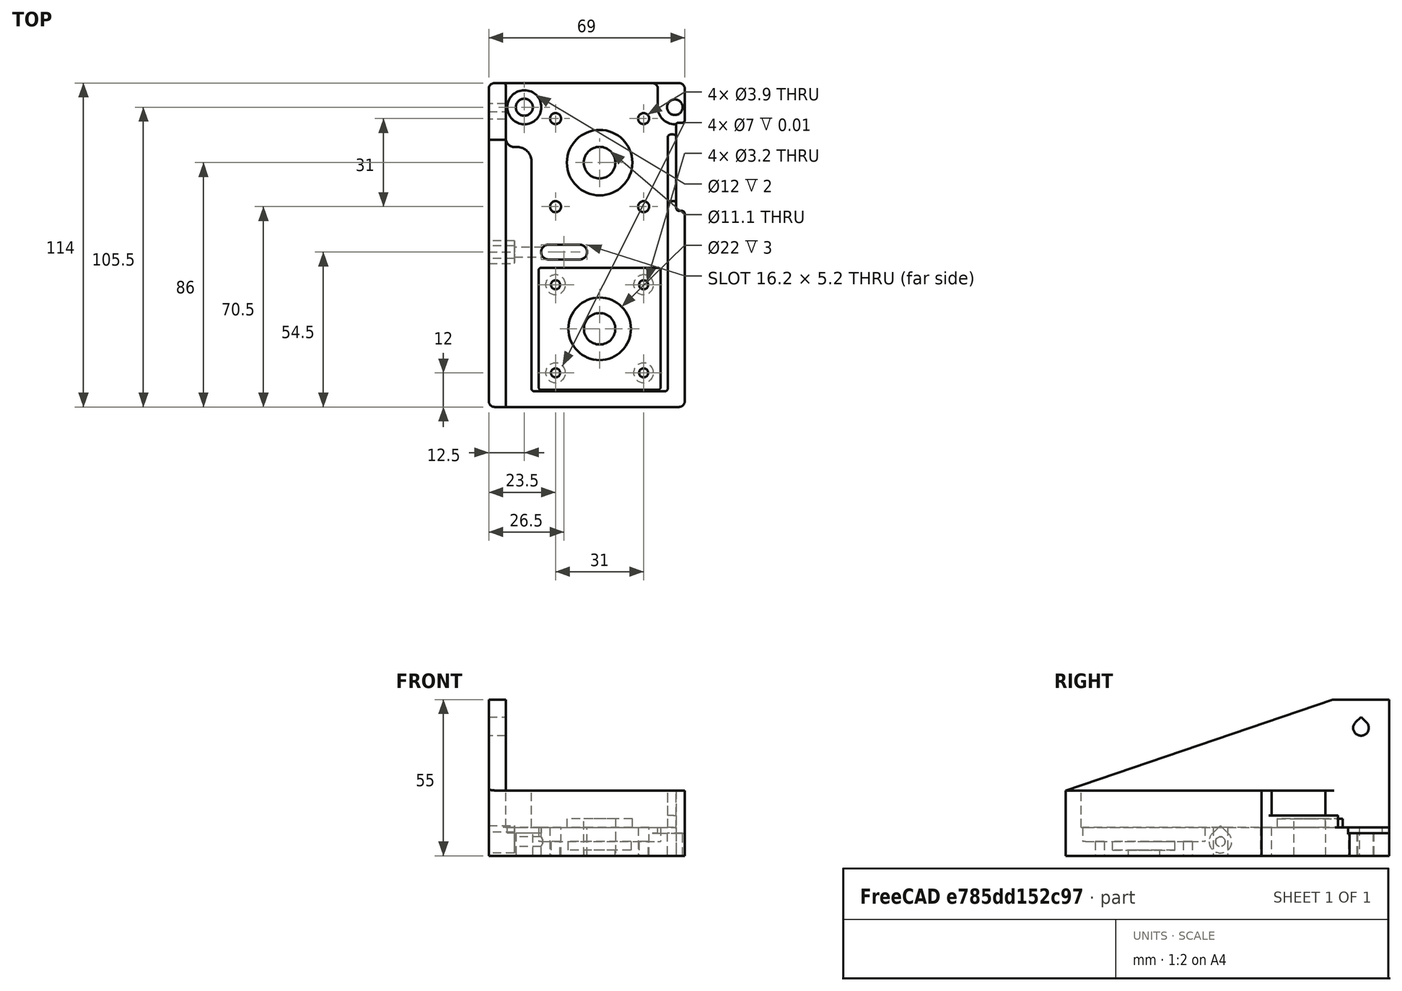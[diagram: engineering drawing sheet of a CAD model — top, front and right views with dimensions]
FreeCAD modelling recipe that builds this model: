
FCSTD DOCUMENT  (FreeCAD 0.19R)
Label: BeltDriveUnit4
License: All rights reserved
LicenseURL: http://en.wikipedia.org/wiki/All_rights_reserved
objects: Sketcher::SketchObject×17, PartDesign::Pocket×12, PartDesign::Fillet×12, PartDesign::Pad×5, PartDesign::Body×1, Mesh::Feature×1
note: 76 computed .brp shape members not serialized (recipe doc carries the construction recipe); baked Part::Feature solids carry a one-line shape summary decoded from their .brp

FEATURE [Sketcher::SketchObject] Sketch
  FullyConstrained = false
  MapMode = 5
  Support = -> [XY_Plane]
  sketch-geometry (17):
    g0: LineSegment StartX=-33 StartY=28 StartZ=0 EndX=30 EndY=28 EndZ=0
    g1: LineSegment StartX=30 StartY=28 StartZ=0 EndX=30 EndY=-86 EndZ=0
    g2: LineSegment StartX=30 StartY=-86 StartZ=0 EndX=-33 EndY=-86 EndZ=0
    g3: LineSegment StartX=-33 StartY=-86 StartZ=0 EndX=-33 EndY=28 EndZ=0
    g4: LineSegment StartX=-21 StartY=21 StartZ=0 EndX=21 EndY=21 EndZ=0
    g5: LineSegment StartX=21 StartY=21 StartZ=0 EndX=21 EndY=-21 EndZ=0
    g6: LineSegment StartX=21 StartY=-21 StartZ=0 EndX=-21 EndY=-21 EndZ=0
    g7: LineSegment StartX=-21 StartY=-21 StartZ=0 EndX=-21 EndY=21 EndZ=0
    g8: Circle CenterX=-15.5 CenterY=15.5 CenterZ=0 NormalX=0 NormalY=0 NormalZ=1 AngleXU=0 Radius=1.95
    g9: Circle CenterX=15.5 CenterY=15.5 CenterZ=0 NormalX=0 NormalY=0 NormalZ=1 AngleXU=0 Radius=1.95
    g10: Circle CenterX=-15.5 CenterY=-15.5 CenterZ=0 NormalX=0 NormalY=0 NormalZ=1 AngleXU=0 Radius=1.95
    g11: Circle CenterX=15.5 CenterY=-15.5 CenterZ=0 NormalX=0 NormalY=0 NormalZ=1 AngleXU=0 Radius=1.95
    g12: Circle CenterX=0 CenterY=-58.5 CenterZ=0 NormalX=0 NormalY=0 NormalZ=1 AngleXU=0 Radius=5.525
    g13: Circle CenterX=-15.5 CenterY=-43 CenterZ=0 NormalX=0 NormalY=0 NormalZ=1 AngleXU=0 Radius=1.6
    g14: Circle CenterX=15.5 CenterY=-43 CenterZ=0 NormalX=0 NormalY=0 NormalZ=1 AngleXU=0 Radius=1.6
    g15: Circle CenterX=-15.5 CenterY=-74 CenterZ=0 NormalX=0 NormalY=0 NormalZ=1 AngleXU=0 Radius=1.6
    g16: Circle CenterX=15.5 CenterY=-74 CenterZ=0 NormalX=0 NormalY=0 NormalZ=1 AngleXU=0 Radius=1.6
  constraints (44):
    c: Coincident(g0,g1)
    c: Coincident(g1,g2)
    c: Coincident(g2,g3)
    c: Coincident(g3,g0)
    c: Horizontal(g2)
    c: Vertical(g1)
    c: Vertical(g3)
    c: Coincident(g4,g5)
    c: Coincident(g5,g6)
    c: Coincident(g6,g7)
    c: Coincident(g7,g4)
    c: Horizontal(g4)
    c: Horizontal(g6)
    c: Vertical(g5)
    c: Vertical(g7)
    c: Equal(g5,g4)
    c: Distance(g5) = 42
    c: Symmetric(g4,g6,g-1)
    c: Distance(g4,g0) = 7
    c: Diameter(g11) = 3.9
    c: Equal(g11,g10)
    c: Equal(g11,g8)
    c: Equal(g11,g9)
    c: Distance(g9,g8) = 31
    c: Symmetric(g9,g8,g-2)
    c: Distance(g10,g8) = 31
    c: DistanceY(g11,g9) = 31
    c: DistanceX(g10,g11) = 31
    c: Symmetric(g9,g10,g-1)
    c: Diameter(g16) = 3.2
    c: Equal(g16,g14)
    c: Equal(g16,g13)
    c: Equal(g16,g15)
    c: Symmetric(g14,g13,g-2)
    c: Symmetric(g16,g15,g-2)
    c: Symmetric(g16,g13,g12)
    c: PointOnObject(g12,g-2)
    c: Distance(g14,g13) = 31
    c: Distance(g16,g14) = 31
    c: Distance(g-1,g12) = 58.5
    c: Diameter(g12) = 11.05
    c: DistanceY(g1) = -86
    c: DistanceX(g0) = 30
    c: DistanceX(g0) = -33
FEATURE [PartDesign::Pad] Pad
  Direction = (1,1,1)
  Length = 10
  Length2 = 100
  Profile = -> Sketch
  Type = 0
FEATURE [Sketcher::SketchObject] Sketch004  label="StepperPlugArtillery"
  FullyConstrained = true
  MapMode = 5
  Placement = pos=(0,0,10) rot=(0,0,1;0rad)
  Support = -> [Pad]
  sketch-geometry (1):
    g0: Circle CenterX=0 CenterY=0 CenterZ=0 NormalX=0 NormalY=0 NormalZ=1 AngleXU=0 Radius=11.525
  constraints (2):
    c: Coincident(g0,g-1)
    c: Diameter(g0) = 23.05
FEATURE [PartDesign::Pad] Pad001
  BaseFeature = -> Pad
  Direction = (1,1,1)
  Length = 3
  Length2 = 100
  Profile = -> Sketch004
  Type = 0
FEATURE [Sketcher::SketchObject] Sketch003  label="BearingBore"
  FullyConstrained = false
  MapMode = 5
  Placement = pos=(0,0,13) rot=(0,0,1;0rad)
  Support = -> [Pad001]
  sketch-geometry (1):
    g0: Circle CenterX=0 CenterY=0 CenterZ=0 NormalX=0 NormalY=0 NormalZ=1 AngleXU=0 Radius=5.55
  constraints (1):
    c: Diameter(g0) = 11.1
FEATURE [PartDesign::Pocket] Pocket
  BaseFeature = -> Pad001
  Length = 5
  Length2 = 100
  Profile = -> Sketch003
  Type = 1
FEATURE [Sketcher::SketchObject] Sketch006  label="StepperSocket"
  ExternalGeometry = -> [Pocket]
  FullyConstrained = true
  MapMode = 5
  Placement = pos=(0,0,10) rot=(0,0,1;0rad)
  Support = -> [Pocket]
  sketch-geometry (1):
    g0: Circle CenterX=0 CenterY=-58.5 CenterZ=0 NormalX=0 NormalY=0 NormalZ=1 AngleXU=0 Radius=11
  constraints (2):
    c: Coincident(g0,g-3)
    c: Diameter(g0) = 22
FEATURE [PartDesign::Pocket] Pocket001
  BaseFeature = -> Pocket
  Length = 8
  Length2 = 100
  Profile = -> Sketch006
  Type = 0
FEATURE [Sketcher::SketchObject] Sketch007  label="StepperHolesNot using"
  ExternalGeometry = -> [Pocket001]
  FullyConstrained = true
  MapMode = 5
  Placement = pos=(0,0,0) rot=(1,0,0;3.14159rad)
  Support = -> [Pocket001]
  sketch-geometry (4):
    g0: Circle CenterX=-15.5 CenterY=74 CenterZ=0 NormalX=0 NormalY=0 NormalZ=1 AngleXU=0 Radius=3.5
    g1: Circle CenterX=15.5 CenterY=74 CenterZ=0 NormalX=0 NormalY=0 NormalZ=1 AngleXU=0 Radius=3.5
    g2: Circle CenterX=15.5 CenterY=43 CenterZ=0 NormalX=0 NormalY=0 NormalZ=1 AngleXU=0 Radius=3.5
    g3: Circle CenterX=-15.5 CenterY=43 CenterZ=0 NormalX=0 NormalY=0 NormalZ=1 AngleXU=0 Radius=3.5
  constraints (9):
    c: Diameter(g3) = 7
    c: Equal(g3,g1)
    c: Equal(g3,g2)
    c: Equal(g3,g0)
    c: Symmetric(g0,g2,g-3)
    c: Symmetric(g1,g3,g-3)
    c: Distance(g2,g1) = 31
    c: Distance(g3,g2) = 31
    c: Symmetric(g3,g2,g-2)
FEATURE [PartDesign::Pocket] Pocket002
  BaseFeature = -> Pocket001
  Length = 0.01
  Length2 = 100
  Profile = -> Sketch007
  Type = 0
FEATURE [Sketcher::SketchObject] Sketch008  label="Slot"
  ExternalGeometry = -> [Pocket002]
  FullyConstrained = true
  MapMode = 5
  Placement = pos=(0,0,10) rot=(0,0,1;0rad)
  Support = -> [Pocket002]
  sketch-geometry (11):
    g0: Circle CenterX=0 CenterY=0 CenterZ=0 NormalX=0 NormalY=0 NormalZ=1 AngleXU=0 Radius=18.5
    g1: Circle CenterX=0 CenterY=-58.5 CenterZ=0 NormalX=0 NormalY=0 NormalZ=1 AngleXU=0 Radius=6
    g2: LineSegment StartX=-18.0727 StartY=-3.95299 StartZ=0 EndX=-5.86143 EndY=-59.782 EndZ=0
    g3: ArcOfCircle CenterX=-18 CenterY=-31.5 CenterZ=0 NormalX=0 NormalY=0 NormalZ=1 AngleXU=0 Radius=2.6 StartAngle=1.5708 EndAngle=4.71239
    g4: ArcOfCircle CenterX=-7 CenterY=-31.5 CenterZ=0 NormalX=0 NormalY=0 NormalZ=1 AngleXU=0 Radius=2.6 StartAngle=4.71239 EndAngle=7.85398
    g5: LineSegment StartX=-18 StartY=-34.1 StartZ=0 EndX=-7 EndY=-34.1 EndZ=0
    g6: LineSegment StartX=-18 StartY=-28.9 StartZ=0 EndX=-7 EndY=-28.9 EndZ=0
    g7: Circle CenterX=-18 CenterY=-31.5 CenterZ=0 NormalX=0 NormalY=0 NormalZ=1 AngleXU=0 Radius=6
    g8: Circle CenterX=-7 CenterY=-31.5 CenterZ=0 NormalX=0 NormalY=0 NormalZ=1 AngleXU=0 Radius=6
    g9: LineSegment StartX=-15.5 StartY=-37.5 StartZ=0 EndX=-15.5 EndY=-79 EndZ=0
    g10: LineSegment StartX=-15.5 StartY=-31.5 StartZ=0 EndX=-15.5 EndY=-37.5 EndZ=0
  constraints (29):
    c: Diameter(g0) = 37
    c: Coincident(g0,g-1)
    c: Diameter(g1) = 12
    c: Coincident(g1,g-3)
    c: PointOnObject(g2,g0)
    c: PointOnObject(g2,g1)
    c: Tangent(g2,g0)
    c: Tangent(g1,g2)
    c: Tangent(g3,g6) = 1.5708
    c: Tangent(g3,g5) = -1.5708
    c: Tangent(g5,g4) = -1.5708
    c: Tangent(g6,g4) = 1.5708
    c: Horizontal(g5)
    c: Equal(g3,g4)
    c: Diameter(g7) = 12
    c: Coincident(g3,g7)
    c: Diameter(g8) = 12
    c: Coincident(g8,g4)
    c: Distance(g3,g3) = 5.2
    c: Distance(g6) = 11
    c: DistanceX(g4) = -7
    c: Vertical(g9)
    c: Distance(g9) = 41.5
    c: PointOnObject(g-5,g9)
    c: DistanceY(g-5,g9) = 5.5
    c: Vertical(g10)
    c: Distance(g10) = 6
    c: Coincident(g10,g9)
    c: DistanceY(g10,g3) = 0
FEATURE [PartDesign::Pocket] Pocket003
  BaseFeature = -> Pocket002
  Length = 5
  Length2 = 100
  Profile = -> Sketch008
  Type = 1
FEATURE [Sketcher::SketchObject] Sketch009  label="JackScrew"
  FullyConstrained = true
  MapMode = 5
  Placement = pos=(-33,0,0) rot=(0.57735,-0.57735,-0.57735;2.0944rad)
  Support = -> [Pocket003]
  sketch-geometry (1):
    g0: Circle CenterX=31.5 CenterY=5 CenterZ=0 NormalX=0 NormalY=0 NormalZ=1 AngleXU=0 Radius=1.7
  constraints (3):
    c: Diameter(g0) = 3.4
    c: DistanceY(g0) = 5
    c: DistanceX(g0) = 31.5
FEATURE [PartDesign::Pocket] Pocket004
  BaseFeature = -> Pocket003
  Length = 17
  Length2 = 100
  Profile = -> Sketch009
  Type = 0
FEATURE [Sketcher::SketchObject] Sketch014  label="Stiffernerring"
  ExternalGeometry = -> [Pocket004]
  FullyConstrained = true
  MapMode = 5
  Placement = pos=(0,0,10) rot=(0,0,1;0rad)
  Support = -> [Pocket004]
  sketch-geometry (8):
    g0: LineSegment StartX=-33 StartY=5.5 StartZ=0 EndX=-24 EndY=5.5 EndZ=0
    g1: LineSegment StartX=-24 StartY=5.5 StartZ=0 EndX=-24 EndY=-80.5 EndZ=0
    g2: LineSegment StartX=-24 StartY=-80.5 StartZ=0 EndX=24 EndY=-80.5 EndZ=0
    g3: LineSegment StartX=24 StartY=-80.5 StartZ=0 EndX=24 EndY=-13.5 EndZ=0
    g4: LineSegment StartX=24 StartY=-13.5 StartZ=0 EndX=30 EndY=-13.5 EndZ=0
    g5: LineSegment StartX=30 StartY=-13.5 StartZ=0 EndX=30 EndY=-86 EndZ=0
    g6: LineSegment StartX=30 StartY=-86 StartZ=0 EndX=-33 EndY=-86 EndZ=0
    g7: LineSegment StartX=-33 StartY=-86 StartZ=0 EndX=-33 EndY=5.5 EndZ=0
  constraints (22):
    c: Coincident(g0,g1)
    c: Vertical(g1)
    c: Coincident(g1,g2)
    c: Horizontal(g2)
    c: Coincident(g2,g3)
    c: Vertical(g3)
    c: Coincident(g3,g4)
    c: Coincident(g4,g5)
    c: Coincident(g5,g6)
    c: Coincident(g6,g7)
    c: Coincident(g7,g0)
    c: Horizontal(g0)
    c: Distance(g0) = 9
    c: Horizontal(g4)
    c: Distance(g4) = 6
    c: Distance(g2,g6) = 5.5
    c: PointOnObject(g4,g-5)
    c: DistanceY(g-6,g0) = 21
    c: Coincident(g5,g-5)
    c: Coincident(g6,g-4)
    c: Vertical(g7)
    c: DistanceY(g4) = -13.5
FEATURE [PartDesign::Pad] Pad002
  BaseFeature = -> Pocket004
  Direction = (1,1,1)
  Length = 13
  Length2 = 100
  Profile = -> Sketch014
  Type = 0
FEATURE [Sketcher::SketchObject] Sketch022  label="Gussett"
  ExternalGeometry = -> [Pad002]
  FullyConstrained = true
  MapMode = 5
  Placement = pos=(-33,0,0) rot=(0.57735,-0.57735,-0.57735;2.0944rad)
  Support = -> [Pad002]
  sketch-geometry (5):
    g0: LineSegment StartX=-28 StartY=0 StartZ=0 EndX=-28 EndY=55 EndZ=0
    g1: LineSegment StartX=-28 StartY=55 StartZ=0 EndX=-8 EndY=55 EndZ=0
    g2: LineSegment StartX=-8 StartY=55 StartZ=0 EndX=86 EndY=23 EndZ=0
    g3: LineSegment StartX=86 StartY=23 StartZ=0 EndX=86 EndY=0 EndZ=0
    g4: LineSegment StartX=86 StartY=0 StartZ=0 EndX=-28 EndY=0 EndZ=0
  constraints (13):
    c: Vertical(g0)
    c: Coincident(g0,g1)
    c: Horizontal(g1)
    c: Coincident(g1,g2)
    c: Coincident(g2,g3)
    c: Coincident(g4,g0)
    c: Horizontal(g4)
    c: DistanceX(g0) = -28
    c: DistanceY(g0) = 55
    c: DistanceX(g1,g1) = 20
    c: Coincident(g3,g-3)
    c: Coincident(g2,g-4)
    c: Coincident(g4,g3)
FEATURE [PartDesign::Pad] Pad003
  BaseFeature = -> Pad002
  Direction = (1,1,1)
  Length = 6
  Length2 = 100
  Profile = -> Sketch022
  Type = 0
FEATURE [Sketcher::SketchObject] Sketch023  label="GussetBolt"
  ExternalGeometry = -> [Pad003]
  FullyConstrained = true
  MapMode = 5
  Placement = pos=(-39,0,0) rot=(-0.57735,0.57735,0.57735;4.18879rad)
  Support = -> [Pad003]
  sketch-geometry (3):
    g0: ArcOfCircle CenterX=-18 CenterY=45 CenterZ=0 NormalX=0 NormalY=0 NormalZ=1 AngleXU=0 Radius=2.75 StartAngle=2.35619 EndAngle=7.06858
    g1: LineSegment StartX=-19.9445 StartY=46.9445 StartZ=0 EndX=-18 EndY=48.8891 EndZ=0
    g2: LineSegment StartX=-18 StartY=48.8891 StartZ=0 EndX=-16.0555 EndY=46.9445 EndZ=0
  constraints (8):
    c: Coincident(g1,g2)
    c: Tangent(g0,g2) = 1.5708
    c: Tangent(g1,g0) = 1.5708
    c: Angle(g1,g2) = 1.5708
    c: Angle(g2) = -0.785398
    c: Diameter(g0) = 5.5
    c: DistanceY(g0) = 45
    c: Distance(g0,g-3) = 10
FEATURE [PartDesign::Pocket] Pocket005
  BaseFeature = -> Pad003
  Length = 9
  Length2 = 100
  Profile = -> Sketch023
  Type = 0
FEATURE [Sketcher::SketchObject] Sketch025  label="MountingBolteALlen"
  ExternalGeometry = -> [Pocket005]
  FullyConstrained = true
  MapMode = 5
  Placement = pos=(0,0,0) rot=(1,0,0;3.14159rad)
  Support = -> [Pocket005]
  sketch-geometry (2):
    g0: Circle CenterX=26.5 CenterY=-19.5 CenterZ=0 NormalX=0 NormalY=0 NormalZ=1 AngleXU=0 Radius=2.75
    g1: Circle CenterX=-26.5 CenterY=-19.5 CenterZ=0 NormalX=0 NormalY=0 NormalZ=1 AngleXU=0 Radius=3
  constraints (5):
    c: Diameter(g0) = 5.5
    c: DistanceX(g-3,g0) = 11
    c: DistanceY(g0,g-3) = 4
    c: Symmetric(g0,g1,g-2)
    c: Diameter(g1) = 6
FEATURE [PartDesign::Pocket] Pocket006
  BaseFeature = -> Pocket005
  Length = 16
  Length2 = 100
  Profile = -> Sketch025
  Type = 0
FEATURE [Sketcher::SketchObject] Sketch026  label="MountingBoltReleifs"
  ExternalGeometry = -> [Pocket006]
  FullyConstrained = true
  MapMode = 5
  Placement = pos=(0,0,10) rot=(0,0,1;0rad)
  Support = -> [Pocket006]
  sketch-geometry (5):
    g0: ArcOfCircle CenterX=26.5 CenterY=19.5 CenterZ=0 NormalX=0 NormalY=0 NormalZ=1 AngleXU=0 Radius=6 StartAngle=3.14159 EndAngle=4.71239
    g1: Circle CenterX=-26.5 CenterY=19.5 CenterZ=0 NormalX=0 NormalY=0 NormalZ=1 AngleXU=0 Radius=6
    g2: LineSegment StartX=26.5 StartY=13.5 StartZ=0 EndX=46.5 EndY=13.5 EndZ=0
    g3: LineSegment StartX=20.5 StartY=46.38 StartZ=0 EndX=20.5 EndY=19.5 EndZ=0
    g4: LineSegment StartX=20.5 StartY=46.38 StartZ=0 EndX=46.5 EndY=13.5 EndZ=0
  constraints (12):
    c: Coincident(g1,g-3)
    c: Diameter(g1) = 12
    c: Diameter(g0) = 12
    c: Tangent(g0,g2) = -1.5708
    c: Horizontal(g2)
    c: Tangent(g3,g0) = -1.5708
    c: Coincident(g0,g-4)
    c: Distance(g2) = 20
    c: Vertical(g3)
    c: Coincident(g4,g3)
    c: Coincident(g4,g2)
    c: Distance(g3) = 26.88
FEATURE [PartDesign::Pocket] Pocket007
  BaseFeature = -> Pocket006
  Length = 2
  Length2 = 100
  Profile = -> Sketch026
  Type = 0
FEATURE [Sketcher::SketchObject] Sketch027  label="JackScrewspace"
  FullyConstrained = true
  MapMode = 5
  Placement = pos=(-39,0,0) rot=(-0.57735,0.57735,0.57735;4.18879rad)
  Support = -> [Pocket007]
  sketch-geometry (1):
    g0: Circle CenterX=31.5 CenterY=5 CenterZ=0 NormalX=0 NormalY=0 NormalZ=1 AngleXU=0 Radius=4
  constraints (3):
    c: DistanceX(g-1,g0) = 31.5
    c: DistanceY(g0) = 5
    c: Diameter(g0) = 8
FEATURE [PartDesign::Pocket] Pocket008
  BaseFeature = -> Pocket007
  Length = 9
  Length2 = 100
  Profile = -> Sketch027
  Type = 0
FEATURE [Sketcher::SketchObject] Sketch028  label="StepperSocket001"
  ExternalGeometry = -> [Pocket008]
  FullyConstrained = true
  MapMode = 5
  Placement = pos=(0,0,10) rot=(0,0,1;0rad)
  Support = -> [Pocket008]
  sketch-geometry (4):
    g0: LineSegment StartX=-21.5 StartY=-37 StartZ=0 EndX=21.5 EndY=-37 EndZ=0
    g1: LineSegment StartX=21.5 StartY=-37 StartZ=0 EndX=21.5 EndY=-80 EndZ=0
    g2: LineSegment StartX=21.5 StartY=-80 StartZ=0 EndX=-21.5 EndY=-80 EndZ=0
    g3: LineSegment StartX=-21.5 StartY=-80 StartZ=0 EndX=-21.5 EndY=-37 EndZ=0
  constraints (11):
    c: Coincident(g0,g1)
    c: Coincident(g1,g2)
    c: Coincident(g2,g3)
    c: Coincident(g3,g0)
    c: Horizontal(g2)
    c: Vertical(g1)
    c: Vertical(g3)
    c: Equal(g0,g3)
    c: Distance(g0) = 43
    c: Perpendicular(g0,g3)
    c: Symmetric(g1,g0,g-4)
FEATURE [PartDesign::Pocket] Pocket009
  BaseFeature = -> Pocket008
  Length = 5
  Length2 = 100
  Profile = -> Sketch028
  Type = 0
FEATURE [Sketcher::SketchObject] Sketch029
  FullyConstrained = true
  MapMode = 5
  Placement = pos=(0,0,23) rot=(0,0,1;0rad)
  Support = -> [Pocket009]
  sketch-geometry (4):
    g0: LineSegment StartX=34.97 StartY=14 StartZ=0 EndX=27 EndY=14 EndZ=0
    g1: LineSegment StartX=27 StartY=14 StartZ=0 EndX=27 EndY=-17 EndZ=0
    g2: LineSegment StartX=27 StartY=-17 StartZ=0 EndX=34.97 EndY=-17 EndZ=0
    g3: LineSegment StartX=34.97 StartY=-17 StartZ=0 EndX=34.97 EndY=14 EndZ=0
  constraints (12):
    c: Coincident(g0,g1)
    c: Coincident(g1,g2)
    c: Coincident(g2,g3)
    c: Coincident(g3,g0)
    c: Horizontal(g0)
    c: Horizontal(g2)
    c: Vertical(g1)
    c: Vertical(g3)
    c: DistanceX(g0) = 27
    c: DistanceY(g0) = 14
    c: DistanceY(g1) = -17
    c: Distance(g0) = 7.97
FEATURE [PartDesign::Pocket] Pocket010
  BaseFeature = -> Pocket009
  Length = 28
  Length2 = 100
  Profile = -> Sketch029
  Type = 0
FEATURE [Sketcher::SketchObject] Sketch030
  FullyConstrained = false
  MapMode = 5
  Placement = pos=(27,0,0) rot=(0.57735,0.57735,0.57735;2.0944rad)
  Support = -> [Pocket010]
  sketch-geometry (4):
    g0: LineSegment StartX=-14.3924 StartY=14.1374 StartZ=0 EndX=9.88868 EndY=14.1374 EndZ=0
    g1: LineSegment StartX=9.88868 StartY=14.1374 StartZ=0 EndX=9.88868 EndY=9.46986 EndZ=0
    g2: LineSegment StartX=9.88868 StartY=9.46986 StartZ=0 EndX=-14.3924 EndY=9.46986 EndZ=0
    g3: LineSegment StartX=-14.3924 StartY=9.46986 StartZ=0 EndX=-14.3924 EndY=14.1374 EndZ=0
  constraints (8):
    c: Coincident(g0,g1)
    c: Coincident(g1,g2)
    c: Coincident(g2,g3)
    c: Coincident(g3,g0)
    c: Horizontal(g0)
    c: Horizontal(g2)
    c: Vertical(g1)
    c: Vertical(g3)
FEATURE [PartDesign::Pad] Pad004
  BaseFeature = -> Pocket010
  Direction = (1,1,1)
  Length = 3
  Length2 = 100
  Profile = -> Sketch030
  Reversed = true
  Type = 0
FEATURE [PartDesign::Fillet] Fillet
  Base = -> Pad004 [Edge2,Edge68,Edge71,Edge148]
  BaseFeature = -> Pad004
  Radius = 2
  SupportTransform = false
FEATURE [PartDesign::Fillet] Fillet001
  Base = -> Fillet [Edge93]
  BaseFeature = -> Fillet
  Radius = 0.5
  SupportTransform = false
FEATURE [PartDesign::Fillet] Fillet002
  Base = -> Fillet001 [Edge43,Edge29,Edge42]
  BaseFeature = -> Fillet001
  Radius = 1
  SupportTransform = false
FEATURE [PartDesign::Fillet] Fillet003
  Base = -> Fillet002 [Edge35,Edge120]
  BaseFeature = -> Fillet002
  Radius = 1
  SupportTransform = false
FEATURE [PartDesign::Fillet] Fillet004
  Base = -> Fillet003 [Edge137]
  BaseFeature = -> Fillet003
  Radius = 2
  SupportTransform = false
FEATURE [PartDesign::Fillet] Fillet005
  Base = -> Fillet004 [Edge70]
  BaseFeature = -> Fillet004
  Radius = 1
  SupportTransform = false
FEATURE [PartDesign::Fillet] Fillet006
  Base = -> Fillet005 [Edge33]
  BaseFeature = -> Fillet005
  Radius = 1
  SupportTransform = false
FEATURE [PartDesign::Fillet] Fillet007
  Base = -> Fillet006 [Edge52]
  BaseFeature = -> Fillet006
  Radius = 0.4
  SupportTransform = false
FEATURE [PartDesign::Fillet] Fillet008
  Base = -> Fillet007 [Edge86]
  BaseFeature = -> Fillet007
  Radius = 5
  SupportTransform = false
FEATURE [PartDesign::Fillet] Fillet009
  Base = -> Fillet008 [Edge36]
  BaseFeature = -> Fillet008
  Radius = 3
  SupportTransform = false
FEATURE [PartDesign::Fillet] Fillet010
  Base = -> Fillet009 [Edge42]
  BaseFeature = -> Fillet009
  Radius = 1
  SupportTransform = false
FEATURE [PartDesign::Fillet] Fillet011
  Base = -> Fillet010 [Edge70,Edge66,Edge107,Edge109,Edge106,Edge104]
  BaseFeature = -> Fillet010
  Radius = 1
  SupportTransform = false
FEATURE [Sketcher::SketchObject] Sketch031
  FullyConstrained = false
  MapMode = 5
  Placement = pos=(-39,0,0) rot=(-0.57735,0.57735,0.57735;4.18879rad)
  Support = -> [Fillet011]
  sketch-geometry (3):
    g0: LineSegment StartX=31.4987 StartY=10.5569 StartZ=0 EndX=28.5212 EndY=7.57942 EndZ=0
    g1: LineSegment StartX=28.5212 StartY=7.57942 StartZ=0 EndX=34.4762 EndY=7.57942 EndZ=0
    g2: LineSegment StartX=34.4762 StartY=7.57942 StartZ=0 EndX=31.4987 EndY=10.5569 EndZ=0
  constraints (6):
    c: Coincident(g0,g1)
    c: Horizontal(g1)
    c: Coincident(g1,g2)
    c: Coincident(g2,g0)
    c: Angle(g0,g2) = 1.5708
    c: Angle(g2) = 2.35619
FEATURE [PartDesign::Pocket] Pocket011
  BaseFeature = -> Fillet011
  Length = 9
  Length2 = 100
  Profile = -> Sketch031
  Type = 0
FEATURE [PartDesign::Body] Body
  Group = -> [Sketch,Pad,Sketch003,Sketch004,Pad001,Pocket,Sketch006,Pocket001,Sketch007,Pocket002,Sketch008,Pocket003,Sketch009,Pocket004,Sketch014,Pad002,Sketch022,Pad003,Sketch023,Pocket005,Sketch025,Pocket006,Sketch026,Pocket007,Sketch027,Pocket008,Sketch028,Pocket009,Sketch029,Pocket010,Sketch030,Pad004,Fillet,Fillet001,Fillet002,Fillet003,Fillet004,Fillet005,Fillet006,Fillet007,Fillet008,Fillet009,+4 more]
  Origin = -> Origin
  Tip = -> Pocket011
FEATURE [Mesh::Feature] Mesh  label="Pocket011 (Meshed)"
